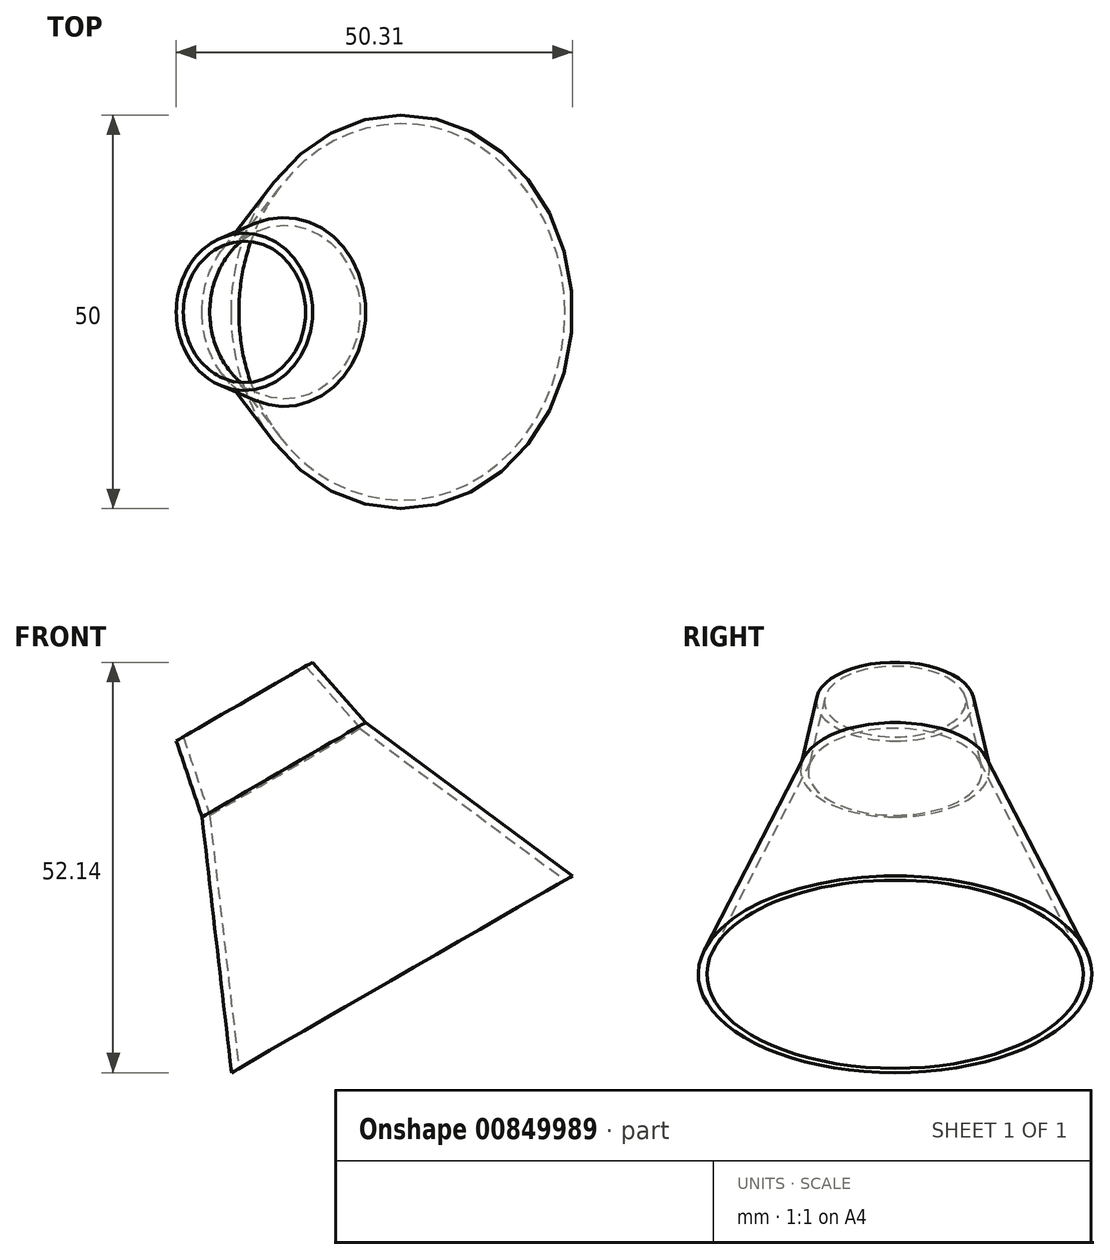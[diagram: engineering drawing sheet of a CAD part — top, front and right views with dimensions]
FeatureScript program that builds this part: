
annotation { "Feature Type Name" : "Feature", "Feature Type Description" : "" }
export const myFeature = defineFeature(function(context is Context, id is Id, definition is map)
    precondition{}
    {
        {
            var Q0;
            Q0=qCreatedBy(makeId("Front.planeOp"),FACE);
            var sketch = newSketch(context, id + "F0", { "sketchPlane" : qUnion([Q0])});
            skLineSegment(sketch, "E0", {"start": v(0, 40) * mm, "end": v(10, 40) * mm});
            skLineSegment(sketch, "E1", {"start": v(25, 0) * mm, "end": v(0, 0) * mm});
            skLineSegment(sketch, "E2", {"start": v(0, 0) * mm, "end": v(0, 40) * mm});
            skLineSegment(sketch, "E3", {"start": v(10, 40) * mm, "end": v(12, 30) * mm});
            skLineSegment(sketch, "E4", {"start": v(12, 30) * mm, "end": v(25, 0) * mm});
            skSolve(sketch);
        }
        {
            var Q0;
            Q0=makeQuery(id+"F0.imprint","IMPRINT",FACE,{"disambiguationData":[TD([[makeQuery(id+"F0.imprint","IMPRINT",EDGE,{"derivedFrom":sQuery(id+"F0.wireOp",EDGE,"E0")}),-1.0]])]});
            var Q1;
            Q1=sQuery(id+"F0.wireOp",EDGE,"E2");
            revolve(context, id + "F1", {"surfaceOperationType" : NewSurfaceOperationType.NEW, "entities" : qUnion([Q0]), "axis" : qUnion([Q1]), "revolveType" : RevolveType.FULL});
        }
        {
            var Q0;
            Q0=makeQuery(id+"F1.opRevolve","SWEPT_FACE",FACE,{"disambiguationData":[OSD([sQuery(id+"F0.wireOp",EDGE,"E1")])]});
            var Q1;
            Q1=makeQuery(id+"F1.opRevolve","SWEPT_FACE",FACE,{"disambiguationData":[OSD([sQuery(id+"F0.wireOp",EDGE,"E0")])]});
            shell(context, id + "F2", {"entities" : qUnion([Q0, Q1]), "thickness" : 1 * mm});
        }
        {
            var Q0;
            Q0=makeQuery(id+"F1.opRevolve","SWEPT_BODY",BODY,{"disambiguationData":[OSD([sQuery(id+"F0.wireOp",EDGE,"E0"),sQuery(id+"F0.wireOp",EDGE,"Cq4XMn6O-Yc0Y-hynX-itsR-kRmhFGDiWvSs"),sQuery(id+"F0.wireOp",EDGE,"E1"),sQuery(id+"F0.wireOp",EDGE,"E2")])]});
            transform(context, id + "F3", {"entities" : qUnion([Q0]), "transformType" : TransformType.TRANSLATION_3D, "dx" : 30 * mm, "dy" : 0 * mm, "dz" : 50 * mm, "makeCopy" : false});
        }
        {
            var Q0;
            Q0=makeQuery(id+"F1.opRevolve","SWEPT_FACE",FACE,{"disambiguationData":[OSD([sQuery(id+"F0.wireOp",EDGE,"E0")])]});
            var sketch = newSketch(context, id + "F4", { "sketchPlane" : qUnion([Q0])});
            skLineSegment(sketch, "E5", {"start": v(30, 8.98) * mm, "end": v(30, -8.98) * mm, "construction": true});
            skPoint(sketch, "E6", {"position": v(30, 0) * mm});
            skSolve(sketch);
        }
        {
            var Q0;
            Q0=makeQuery(id+"F1.opRevolve","SWEPT_BODY",BODY,{"disambiguationData":[OSD([sQuery(id+"F0.wireOp",EDGE,"E0"),sQuery(id+"F0.wireOp",EDGE,"Cq4XMn6O-Yc0Y-hynX-itsR-kRmhFGDiWvSs"),sQuery(id+"F0.wireOp",EDGE,"E1"),sQuery(id+"F0.wireOp",EDGE,"E2")])]});
            var Q1;
            Q1=sQuery(id+"F4.wireOp",EDGE,"E5");
            transform(context, id + "F5", {"entities" : qUnion([Q0]), "transformType" : TransformType.ROTATION, "transformAxis" : qUnion([Q1]), "angle" : 30 * degree, "makeCopy" : false});
        }
    });
